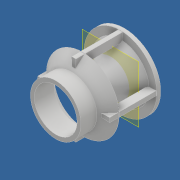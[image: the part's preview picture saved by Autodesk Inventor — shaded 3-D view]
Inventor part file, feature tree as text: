
AUTODESK INVENTOR PART (.ipt)
format: ipt  version: 2017 (Build 210142000, 142)  size: 186,880 bytes
history: native  units: mm
features: sketch x2, revolve x1, plane x1, extrude x1
ambient origin geometry x8: Origin, YZ Plane, XZ Plane, XY Plane, X Axis, Y Axis, Z Axis, Center Point
bodies: Body1 (feature_tree)
feature tree (5):
  revolve  "Revolution3"  [1 undecoded]
  plane  "Work Plane2"
  extrude  "Extrusion7"  Depth=3.5mm
  sketch  "Sketch1"  dims[d2=14.0mm d3=8.3mm]
  sketch  "Sketch13"  dims[d9=1.5mm d28=1.0mm d71=1.5mm d72=3.0mm d74=8.0mm d75=90.0deg d76=-21.25mm d142=17.0mm d150=14.0mm d151=30.805061mm d152=1.22173mm d153=10.5mm d154=1.22173mm d155=5.350032mm d156=5.0mm d157=45.0deg d158=14.25mm d159=4.75mm d160=0.0mm d161=0.0mm d170=3.0mm d171=4.0mm d172=135.0deg d176=3.5mm]
note: 1 required parameter value undecoded (feature->parameter linkage not recoverable at this tier; creation-order binding heuristic only, values carry confidence <= 0.55)
